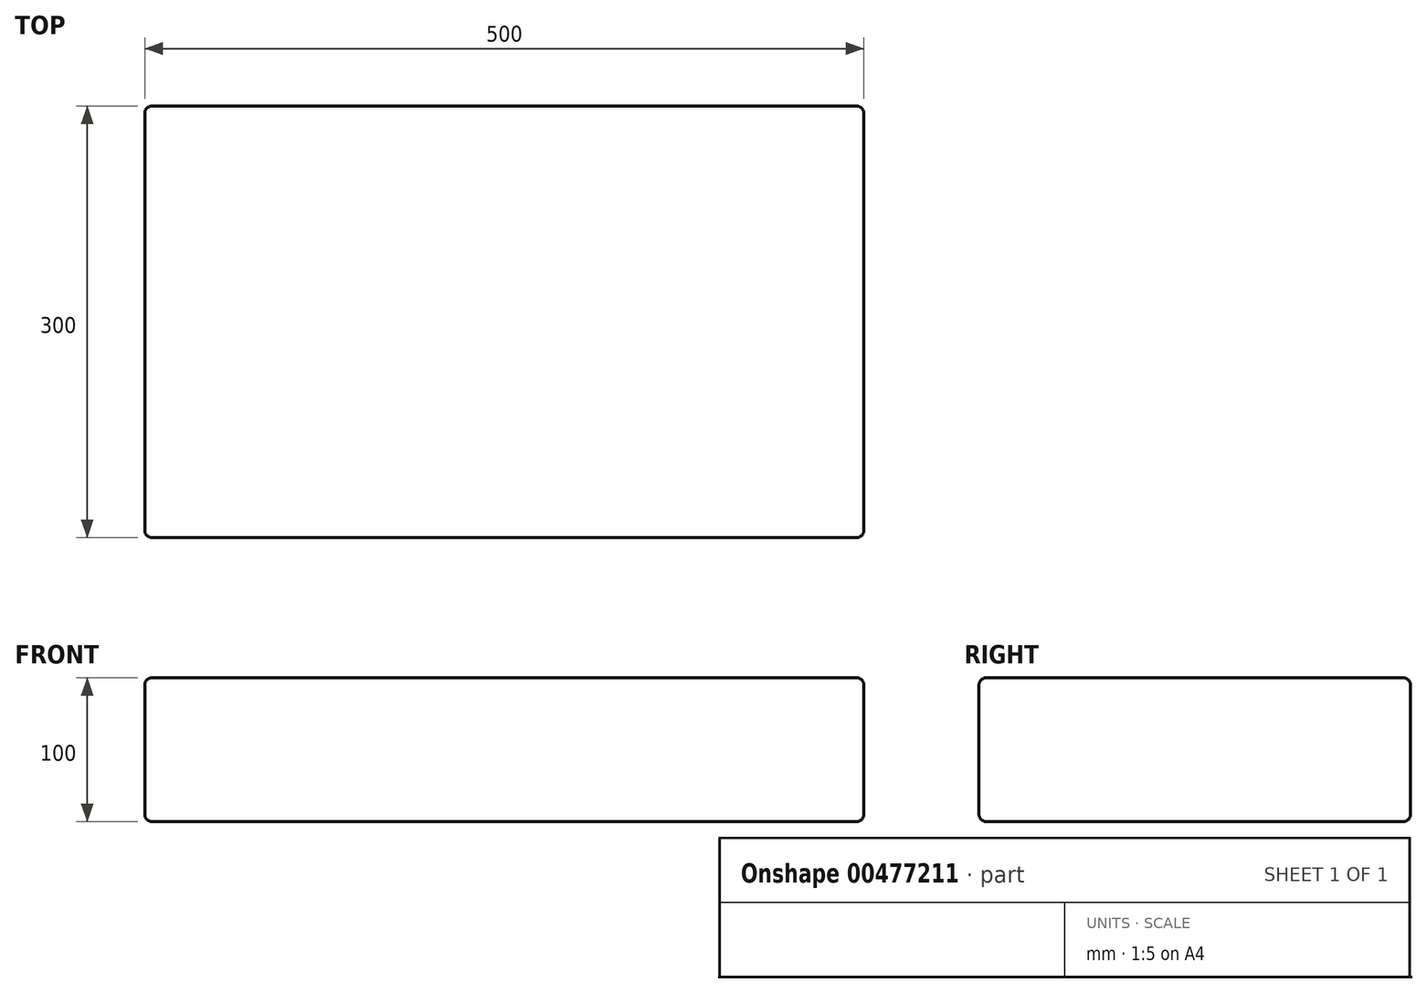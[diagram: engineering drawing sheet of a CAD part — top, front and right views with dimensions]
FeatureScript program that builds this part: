
annotation { "Feature Type Name" : "Feature", "Feature Type Description" : "" }
export const myFeature = defineFeature(function(context is Context, id is Id, definition is map)
    precondition{}
    {
        {
            var Q0;
            Q0=qCreatedBy(makeId("Top.planeOp"),FACE);
            var sketch = newSketch(context, id + "F0", { "sketchPlane" : qUnion([Q0])});
            skLineSegment(sketch, "E0.bottom", {"start": v(-250, -150) * mm, "end": v(250, -150) * mm});
            skLineSegment(sketch, "E0.top", {"start": v(-250, 150) * mm, "end": v(250, 150) * mm});
            skLineSegment(sketch, "E0.left", {"start": v(-250, -150) * mm, "end": v(-250, 150) * mm});
            skLineSegment(sketch, "E0.right", {"start": v(250, -150) * mm, "end": v(250, 150) * mm});
            skPoint(sketch, "E0.middle", {"position": v(0, 0) * mm});
            skSolve(sketch);
        }
        {
            var Q0;
            Q0=makeQuery(id+"F0.imprint","IMPRINT",FACE,{"disambiguationData":[TD([[makeQuery(id+"F0.imprint","IMPRINT",EDGE,{"derivedFrom":sQuery(id+"F0.wireOp",EDGE,"E0.bottom")}),1.0]])]});
            extrude(context, id + "F1", {"entities" : qUnion([Q0]), "depth" : 100 * mm});
        }
        {
            var Q0;
            Q0=makeQuery(id+"F1.opExtrude","CAP_FACE",FACE,{"disambiguationData":[OSD([sQuery(id+"F0.wireOp",EDGE,"E0.bottom"),sQuery(id+"F0.wireOp",EDGE,"E0.top"),sQuery(id+"F0.wireOp",EDGE,"E0.left"),sQuery(id+"F0.wireOp",EDGE,"E0.right")])],"isStart":false});
            var Q1;
            Q1=makeQuery(id+"F1.opExtrude","SWEPT_FACE",FACE,{"disambiguationData":[OSD([sQuery(id+"F0.wireOp",EDGE,"E0.right")])]});
            var Q2;
            Q2=makeQuery(id+"F1.opExtrude","CAP_FACE",FACE,{"disambiguationData":[OSD([sQuery(id+"F0.wireOp",EDGE,"E0.bottom"),sQuery(id+"F0.wireOp",EDGE,"E0.top"),sQuery(id+"F0.wireOp",EDGE,"E0.left"),sQuery(id+"F0.wireOp",EDGE,"E0.right")])],"isStart":true});
            var Q3;
            Q3=makeQuery(id+"F1.opExtrude","SWEPT_FACE",FACE,{"disambiguationData":[OSD([sQuery(id+"F0.wireOp",EDGE,"E0.left")])]});
            fillet(context, id + "F2", {"entities" : qUnion([Q0, Q1, Q2, Q3]), "radius" : 5 * mm, "tangentPropagation" : true, "allowEdgeOverflow" : false});
        }
    });
